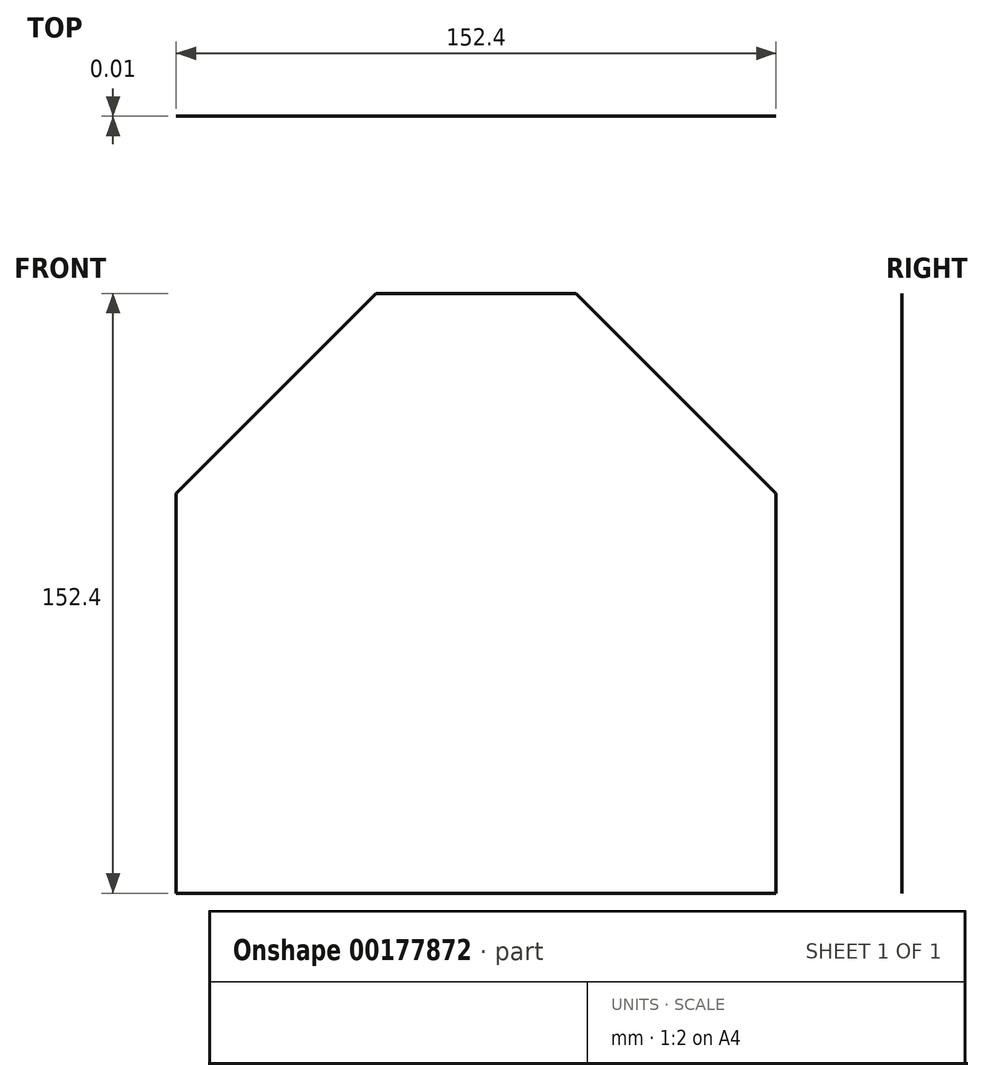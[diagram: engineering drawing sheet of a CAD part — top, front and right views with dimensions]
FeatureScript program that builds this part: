
annotation { "Feature Type Name" : "Feature", "Feature Type Description" : "" }
export const myFeature = defineFeature(function(context is Context, id is Id, definition is map)
    precondition{}
    {
        {
            var Q0;
            Q0=qCreatedBy(makeId("Front.planeOp"),FACE);
            var sketch = newSketch(context, id + "F0", { "sketchPlane" : qUnion([Q0])});
            skLineSegment(sketch, "E0.bottom", {"start": v(25.4, 76.2) * mm, "end": v(-25.4, 76.2) * mm});
            skLineSegment(sketch, "E0.top", {"start": v(76.2, -76.2) * mm, "end": v(-76.2, -76.2) * mm});
            skLineSegment(sketch, "E0.left", {"start": v(76.2, 25.4) * mm, "end": v(76.2, -76.2) * mm});
            skLineSegment(sketch, "E0.right", {"start": v(-76.2, 25.4) * mm, "end": v(-76.2, -76.2) * mm});
            skPoint(sketch, "E0.middle", {"position": v(0, 0) * mm});
            skLineSegment(sketch, "E1", {"start": v(-76.2, 25.4) * mm, "end": v(-25.4, 76.2) * mm});
            skLineSegment(sketch, "E2", {"start": v(-25.4, 76.2) * mm, "end": v(25.4, 76.2) * mm});
            skLineSegment(sketch, "E3", {"start": v(25.4, 76.2) * mm, "end": v(76.2, 25.4) * mm});
            skPoint(sketch, "E4.orphan", {"position": v(-76.2, 76.2) * mm});
            skPoint(sketch, "E5.orphan", {"position": v(76.2, 76.2) * mm});
            skSolve(sketch);
        }
        {
            var Q0;
            Q0 = qSketchRegion(id + "F0", true);
            extrude(context, id + "F1", {"entities" : qUnion([Q0]), "depth" : 3 / 203.2 * mm});
        }
    });
